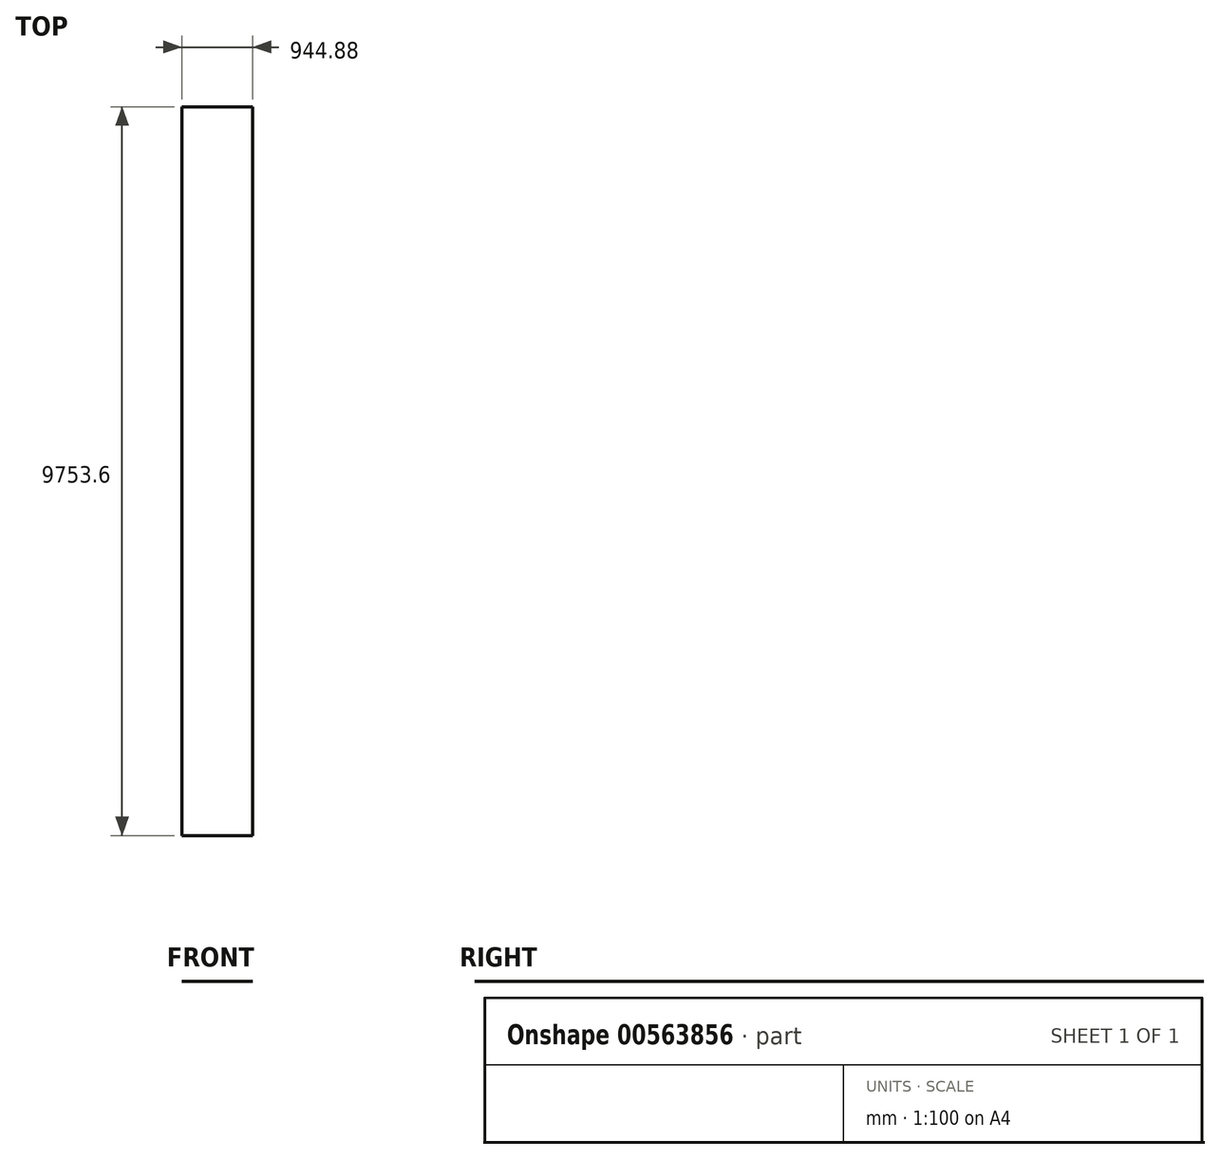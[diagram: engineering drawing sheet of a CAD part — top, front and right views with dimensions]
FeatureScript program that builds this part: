
annotation { "Feature Type Name" : "Feature", "Feature Type Description" : "" }
export const myFeature = defineFeature(function(context is Context, id is Id, definition is map)
    precondition{}
    {
        {
            var Q0;
            Q0=qCreatedBy(makeId("Right.planeOp"),FACE);
            var sketch = newSketch(context, id + "F0", { "sketchPlane" : qUnion([Q0])});
            skLineSegment(sketch, "E0.bottom", {"start": v(-4877.73, -3583.3) * mm, "end": v(4875.87, -3583.3) * mm});
            skLineSegment(sketch, "E0.top", {"start": v(-4877.73, 3583.87) * mm, "end": v(4875.87, 3583.87) * mm});
            skLineSegment(sketch, "E0.left", {"start": v(-4877.73, -3583.3) * mm, "end": v(-4877.73, 3583.87) * mm});
            skLineSegment(sketch, "E0.right", {"start": v(4875.87, -3583.3) * mm, "end": v(4875.87, 3583.87) * mm});
            skSolve(sketch);
        }
        {
            var Q0;
            Q0=sQuery(id+"F0.wireOp",EDGE,"E0.top");
            extrude(context, id + "F1", {"bodyType" : ToolBodyType.SURFACE, "surfaceEntities" : qUnion([Q0]), "depth" : 944.88 * mm, "offsetDistance" : 30.48 * mm});
        }
    });
